# Revit family: Haworth_CabanaLounge_Retreat_Half-BackSofa
name_source: partatom
category: Furniture
revit_build: Autodesk Revit 2018 (Build: 20170223_1515(x64)
units: mm (PartAtom-declared; Revit-internal decimal feet)

## family parameters
Always vertical = Yes
Cut with Voids When Loaded = No
OmniClass Number = 23.40.70.14.64.21
OmniClass Title = Systems Furniture
Room Calculation Point = No
Shared = No
Work Plane-Based = No

## types (6) — shared parameters
Actual Depth = 32"
Actual Width = 104"
Assembly Code = E2020200
Back Width = 42"
Leg Offset = 2 3/4"
Manufacturer = Haworth
Model = Haworth Cabana
Rectangle Control = No
Revision Number = 1
Screen Width = 74"
Seat Depth = 30"
Seat Height = 18 1/16"
Seat Width = 72"
Size = Verify Final Dim. w/ Haworth
Square Control = Yes
Table Width = 30"
URL = http://www.haworth.com
URL - Product = https://www.haworth.com
Warranty = http://www.haworth.com

## per-type parameters (varying)
| type | Actual Height | Description | High Screen | Low Screen | Tiered Top | With Top |
| S9FH-H - High Screen - With Integrated Table - With Tiered Top | 54" | Haworth Cabana Half-Back Sofa Retreat - High Screen - With Integrated Table - With Tiered Top | Yes | No | Yes | Yes |
| S9FH-H - High Screen - With Integrated Table - Without Tiered Top | 54" | Haworth Cabana Half-Back Sofa Retreat - High Screen - With Integrated Table - Without Tiered Top | Yes | No | No | Yes |
| S9FH-H - High Screen - Without Integrated Table - Without Tiered Top | 54" | Haworth Cabana Half-Back Sofa Retreat - High Screen - Without Integrated Table - Without Tiered Top | Yes | No | No | No |
| S9FH-L - Low Screen - With Integrated Table - With Tiered Top | 42" | Haworth Cabana Half-Back Sofa Retreat - Low Screen - With Integrated Table - With Tiered Top | No | Yes | Yes | Yes |
| S9FH-L - Low Screen - With Integrated Table - Without Tiered Top | 42" | Haworth Cabana Half-Back Sofa Retreat - Low Screen - With Integrated Table - Without Tiered Top | No | Yes | No | Yes |
| S9FH-L - Low Screen - Without Integrated Table - Without Tiered Top | 42" | Haworth Cabana Half-Back Sofa Retreat - Low Screen - Without Integrated Table - Without Tiered Top | No | Yes | No | No |

## geometry (parser evidence)
native form markers: Extrusion x4, Sweep x17
no freeform markers — native parametric forms only
